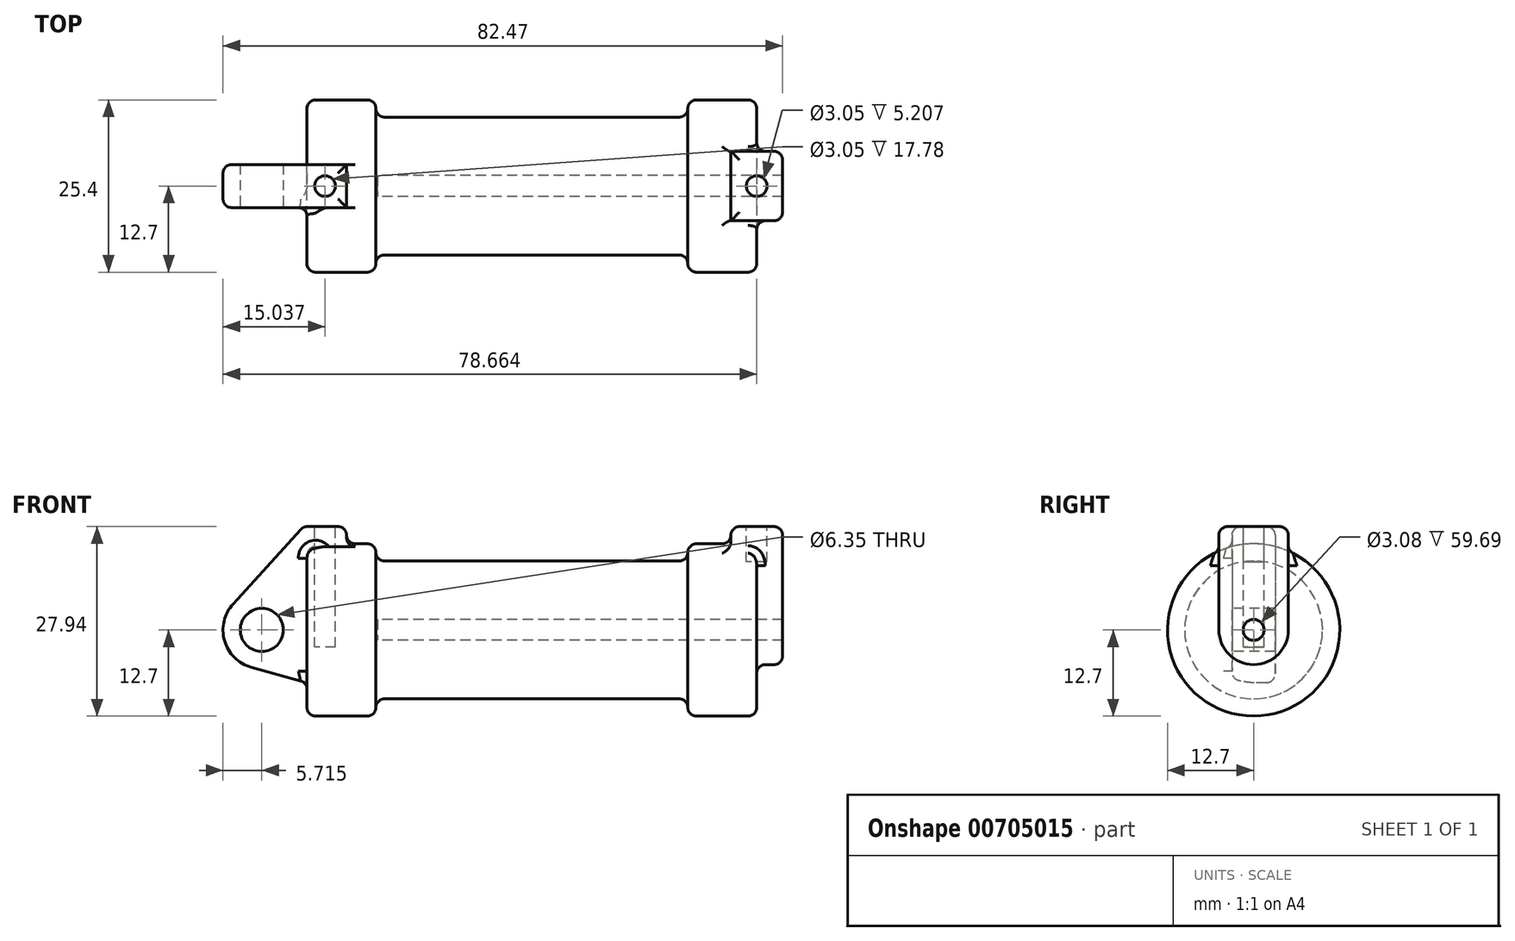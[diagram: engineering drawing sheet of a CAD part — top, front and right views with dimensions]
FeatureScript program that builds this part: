
annotation { "Feature Type Name" : "Feature", "Feature Type Description" : "" }
export const myFeature = defineFeature(function(context is Context, id is Id, definition is map)
    precondition{}
    {
        {
            var Q0;
            Q0=qCreatedBy(makeId("Front.planeOp"),FACE);
            var sketch = newSketch(context, id + "F0", { "sketchPlane" : qUnion([Q0])});
            skLineSegment(sketch, "E0", {"start": v(0, 0) * mm, "end": v(0, 12.7) * mm});
            skLineSegment(sketch, "E1", {"start": v(0, 12.7) * mm, "end": v(10.16, 12.7) * mm});
            skLineSegment(sketch, "E2", {"start": v(10.16, 12.7) * mm, "end": v(10.16, 10.16) * mm});
            skLineSegment(sketch, "E3", {"start": v(10.16, 10.16) * mm, "end": v(56.13, 10.16) * mm});
            skLineSegment(sketch, "E4", {"start": v(56.13, 10.16) * mm, "end": v(56.13, 12.7) * mm});
            skLineSegment(sketch, "E5", {"start": v(56.13, 12.7) * mm, "end": v(66.3, 12.7) * mm});
            skLineSegment(sketch, "E6", {"start": v(66.3, 12.7) * mm, "end": v(66.3, 0) * mm});
            skLineSegment(sketch, "E7", {"start": v(66.3, 0) * mm, "end": v(0, 0) * mm});
            skLineSegment(sketch, "E8", {"start": v(5.84, 15.24) * mm, "end": v(-0.5, 15.24) * mm});
            skLineSegment(sketch, "E9", {"start": v(-0.5, 15.24) * mm, "end": v(-10.88, 3.85) * mm});
            skLineSegment(sketch, "E10", {"start": v(0, 0) * mm, "end": v(-6.65, 0) * mm});
            skCircle(sketch, "E11", {"center": v(-6.65, 0) * mm, "radius": 5.72 * mm});
            skCircle(sketch, "E12", {"center": v(-6.65, 0) * mm, "radius": 3.18 * mm});
            skLineSegment(sketch, "E13", {"start": v(5.84, 15.24) * mm, "end": v(5.84, -9.4) * mm});
            skLineSegment(sketch, "E14", {"start": v(5.84, -9.4) * mm, "end": v(-8.18, -5.5) * mm});
            skSolve(sketch);
        }
        {
            var Q0;
            {var subQ0=sQuery(id+"F0.wireOp",EDGE,"E0");Q0=makeQuery(id+"F0.imprint","IMPRINT",FACE,{"disambiguationData":[TD([[makeQuery(id+"F0.imprint","IMPRINT",EDGE,{"derivedFrom":subQ0}),-1.0]])]});}
            var Q1;
            {var subQ0=sQuery(id+"F0.wireOp",EDGE,"E2");Q1=makeQuery(id+"F0.imprint","IMPRINT",FACE,{"disambiguationData":[TD([[makeQuery(id+"F0.imprint","IMPRINT",EDGE,{"derivedFrom":subQ0}),-1.0]])]});}
            var Q2;
            Q2=sQuery(id+"F0.wireOp",EDGE,"E7");
            revolve(context, id + "F1", {"entities" : qUnion([Q0, Q1]), "axis" : qUnion([Q2]), "revolveType" : RevolveType.FULL});
        }
        {
            var Q0;
            {var subQ1=sQuery(id+"F0.wireOp",EDGE,"E0");Q0=makeQuery(id+"F0.imprint","IMPRINT",FACE,{"disambiguationData":[TD([[makeQuery(id+"F0.imprint","IMPRINT",EDGE,{"derivedFrom":subQ1}),1.0]])]});}
            var Q1;
            {var subQ0=sQuery(id+"F0.wireOp",EDGE,"E14");Q1=makeQuery(id+"F0.imprint","IMPRINT",FACE,{"disambiguationData":[TD([[makeQuery(id+"F0.imprint","IMPRINT",EDGE,{"derivedFrom":subQ0}),-1.0]])]});}
            var Q2;
            {var subQ5=sQuery(id+"F0.wireOp",EDGE,"E12");Q2=makeQuery(id+"F0.imprint","IMPRINT",FACE,{"disambiguationData":[TD([[makeQuery(id+"F0.imprint","IMPRINT",EDGE,{"derivedFrom":subQ5}),-1.0]])]});}
            var Q3;
            {var subQ0=sQuery(id+"F0.wireOp",EDGE,"E0");Q3=makeQuery(id+"F0.imprint","IMPRINT",FACE,{"disambiguationData":[TD([[makeQuery(id+"F0.imprint","IMPRINT",EDGE,{"derivedFrom":subQ0}),-1.0]])]});}
            extrude(context, id + "F2", {"entities" : qUnion([Q0, Q1, Q2, Q3]), "operationType" : NewBodyOperationType.ADD, "oppositeDirection" : true, "depth" : 6.35 * mm, "offsetDistance" : 25.4 * mm, "symmetric" : true});
        }
        {
            var Q0;
            Q0=makeQuery(id+"F1.opRevolve","SWEPT_FACE",FACE,{"disambiguationData":[OSD([sQuery(id+"F0.wireOp",EDGE,"E6")])]});
            var sketch = newSketch(context, id + "F3", { "sketchPlane" : qUnion([Q0])});
            skCircle(sketch, "E15", {"center": v(0, 0) * mm, "radius": 1.54 * mm});
            skCircle(sketch, "E16", {"center": v(0, 0) * mm, "radius": 5.12 * mm});
            skLineSegment(sketch, "E17", {"start": v(-5.12, 0) * mm, "end": v(-5.12, 15.24) * mm});
            skLineSegment(sketch, "E18", {"start": v(5.12, 0) * mm, "end": v(5.12, 15.24) * mm});
            skLineSegment(sketch, "E19", {"start": v(5.12, 15.24) * mm, "end": v(-5.12, 15.24) * mm});
            skSolve(sketch);
        }
        {
            var Q0;
            Q0=makeQuery(id+"F3.imprint","IMPRINT",FACE,{"disambiguationData":[TD([[makeQuery(id+"F3.imprint","IMPRINT",EDGE,{"derivedFrom":sQuery(id+"F3.wireOp",EDGE,"E15")}),-1.0]])]});
            var Q1;
            {var subQ0=sQuery(id+"F3.wireOp",EDGE,"E17");var subQ1=sQuery(id+"F3.wireOp",EDGE,"E16");var subQ2=makeQuery(id+"F3.imprint","INTERSECT",VERTEX,{"derivedFrom":[subQ1,subQ0]});Q1=makeQuery(id+"F3.imprint","IMPRINT",FACE,{"disambiguationData":[TD([[makeQuery(id+"F3.imprint","IMPRINT",EDGE,{"disambiguationData":[TD([[subQ2,1.0]])],"derivedFrom":subQ1}),-1.0]])]});}
            var Q2;
            {var subQ0=sQuery(id+"F3.wireOp",EDGE,"E19");Q2=makeQuery(id+"F3.imprint","IMPRINT",FACE,{"disambiguationData":[TD([[makeQuery(id+"F3.imprint","IMPRINT",EDGE,{"derivedFrom":subQ0}),1.0]])]});}
            extrude(context, id + "F4", {"entities" : qUnion([Q0, Q1, Q2]), "operationType" : NewBodyOperationType.ADD, "depth" : 7.62 * mm, "offsetDistance" : 25.4 * mm, "symmetric" : true});
        }
        {
            var Q0;
            Q0=makeQuery(id+"F4.boolean.opBoolean","SPLIT",FACE,{"disambiguationData":[TD([makeQuery(id+"F4.opExtrude","SWEPT_FACE",FACE,{"disambiguationData":[OSD([sQuery(id+"F3.wireOp",EDGE,"E15")])]})])],"derivedFrom":makeQuery(id+"F1.opRevolve","SWEPT_FACE",FACE,{"disambiguationData":[OSD([sQuery(id+"F0.wireOp",EDGE,"E6")])]})});
            extrude(context, id + "F5", {"entities" : qUnion([Q0]), "operationType" : NewBodyOperationType.REMOVE, "oppositeDirection" : true, "depth" : 55.88 * mm, "offsetDistance" : 25.4 * mm});
        }
        {
            var Q0;
            Q0=makeQuery(id+"F2.opExtrude","SWEPT_FACE",FACE,{"disambiguationData":[OSD([sQuery(id+"F0.wireOp",EDGE,"E8")])]});
            var sketch = newSketch(context, id + "F6", { "sketchPlane" : qUnion([Q0])});
            skPoint(sketch, "E20.centerSnap0", {"position": v(2.67, 3.18) * mm});
            skCircle(sketch, "E21", {"center": v(2.67, 0) * mm, "radius": 1.52 * mm});
            skPoint(sketch, "E21.centerSnap0", {"position": v(-0.5, 0) * mm});
            skSolve(sketch);
        }
        {
            var Q0;
            Q0=makeQuery(id+"F4.opExtrude","SWEPT_FACE",FACE,{"disambiguationData":[OSD([sQuery(id+"F3.wireOp",EDGE,"E19")])]});
            var sketch = newSketch(context, id + "F7", { "sketchPlane" : qUnion([Q0])});
            skCircle(sketch, "E22", {"center": v(66.3, 0) * mm, "radius": 1.52 * mm});
            skPoint(sketch, "E22.centerSnap0", {"position": v(66.3, 5.12) * mm});
            skPoint(sketch, "E22.centerSnap1", {"position": v(62.48, 0) * mm});
            skSolve(sketch);
        }
        {
            var Q0;
            Q0=makeQuery(id+"F7.imprint","IMPRINT",FACE,{"disambiguationData":[TD([[makeQuery(id+"F7.imprint","IMPRINT",EDGE,{"derivedFrom":sQuery(id+"F7.wireOp",EDGE,"E22")}),1.0]])]});
            extrude(context, id + "F8", {"entities" : qUnion([Q0]), "operationType" : NewBodyOperationType.REMOVE, "oppositeDirection" : true, "depth" : 10.4 * mm, "offsetDistance" : 25.4 * mm, "symmetric" : true});
        }
        {
            var Q0;
            Q0=makeQuery(id+"F2.opExtrude","CAP_EDGE",EDGE,{"disambiguationData":[OSD([sQuery(id+"F0.wireOp",EDGE,"E9")])],"isStart":true});
            var Q1;
            Q1=makeQuery(id+"F2.opExtrude","CAP_EDGE",EDGE,{"disambiguationData":[OSD([sQuery(id+"F0.wireOp",EDGE,"E9")])],"isStart":false});
            var Q2;
            Q2=makeQuery(id+"F1.opRevolve","SWEPT_EDGE",EDGE,{"disambiguationData":[OSD([sQuery(id+"F0.wireOp",EDGE,"E0"),sQuery(id+"F0.wireOp",EDGE,"E1")])]});
            var Q3;
            Q3=makeQuery(id+"F2.opExtrude","CAP_EDGE",EDGE,{"disambiguationData":[OSD([sQuery(id+"F0.wireOp",EDGE,"E8")])],"isStart":true});
            var Q4;
            Q4=makeQuery(id+"F2.opExtrude","SWEPT_EDGE",EDGE,{"disambiguationData":[OSD([sQuery(id+"F0.wireOp",EDGE,"E8"),sQuery(id+"F0.wireOp",EDGE,"E13")])]});
            var Q5;
            Q5=makeQuery(id+"F2.opExtrude","CAP_EDGE",EDGE,{"disambiguationData":[OSD([sQuery(id+"F0.wireOp",EDGE,"E8")])],"isStart":false});
            var Q6;
            Q6=makeQuery(id+"F2.opExtrude","SWEPT_EDGE",EDGE,{"disambiguationData":[OSD([sQuery(id+"F0.wireOp",EDGE,"E8"),sQuery(id+"F0.wireOp",EDGE,"E9")])]});
            var Q7;
            Q7=makeQuery(id+"F1.opRevolve","SWEPT_EDGE",EDGE,{"disambiguationData":[OSD([sQuery(id+"F0.wireOp",EDGE,"E1"),sQuery(id+"F0.wireOp",EDGE,"E2")])]});
            var Q8;
            Q8=makeQuery(id+"F4.boolean.opBoolean","INTERSECT",EDGE,{"derivedFrom":[makeQuery(id+"F1.opRevolve","SWEPT_FACE",FACE,{"disambiguationData":[OSD([sQuery(id+"F0.wireOp",EDGE,"E6")])]}),makeQuery(id+"F4.opExtrude","SWEPT_FACE",FACE,{"disambiguationData":[OSD([sQuery(id+"F3.wireOp",EDGE,"E18")])]})]});
            var Q9;
            Q9=makeQuery(id+"F4.opExtrude","CAP_EDGE",EDGE,{"disambiguationData":[OSD([sQuery(id+"F3.wireOp",EDGE,"E18")])],"isStart":false});
            var Q10;
            Q10=makeQuery(id+"F4.opExtrude","CAP_EDGE",EDGE,{"disambiguationData":[OSD([sQuery(id+"F3.wireOp",EDGE,"E19")])],"isStart":false});
            var Q11;
            Q11=makeQuery(id+"F4.opExtrude","SWEPT_EDGE",EDGE,{"disambiguationData":[OSD([sQuery(id+"F3.wireOp",EDGE,"E18"),sQuery(id+"F3.wireOp",EDGE,"E19")])]});
            var Q12;
            Q12=makeQuery(id+"F4.opExtrude","CAP_EDGE",EDGE,{"disambiguationData":[OSD([sQuery(id+"F3.wireOp",EDGE,"E19")])],"isStart":true});
            var Q13;
            Q13=makeQuery(id+"F4.opExtrude","SWEPT_EDGE",EDGE,{"disambiguationData":[OSD([sQuery(id+"F3.wireOp",EDGE,"E17"),sQuery(id+"F3.wireOp",EDGE,"E19")])]});
            var Q14;
            Q14=makeQuery(id+"F4.boolean.opBoolean","INTERSECT",EDGE,{"derivedFrom":[makeQuery(id+"F1.opRevolve","SWEPT_FACE",FACE,{"disambiguationData":[OSD([sQuery(id+"F0.wireOp",EDGE,"E5")])]}),makeQuery(id+"F4.opExtrude","SWEPT_FACE",FACE,{"disambiguationData":[OSD([sQuery(id+"F3.wireOp",EDGE,"E17")])]})]});
            var Q15;
            Q15=makeQuery(id+"F4.boolean.opBoolean","INTERSECT",EDGE,{"derivedFrom":[makeQuery(id+"F1.opRevolve","SWEPT_FACE",FACE,{"disambiguationData":[OSD([sQuery(id+"F0.wireOp",EDGE,"E5")])]}),makeQuery(id+"F4.opExtrude","CAP_FACE",FACE,{"disambiguationData":[OSD([sQuery(id+"F3.wireOp",EDGE,"E15"),sQuery(id+"F3.wireOp",EDGE,"E16"),sQuery(id+"F3.wireOp",EDGE,"E17"),sQuery(id+"F3.wireOp",EDGE,"E18"),sQuery(id+"F3.wireOp",EDGE,"E19")])],"isStart":true})]});
            var Q16;
            Q16=makeQuery(id+"F4.boolean.opBoolean","INTERSECT",EDGE,{"derivedFrom":[makeQuery(id+"F1.opRevolve","SWEPT_FACE",FACE,{"disambiguationData":[OSD([sQuery(id+"F0.wireOp",EDGE,"E5")])]}),makeQuery(id+"F4.opExtrude","SWEPT_FACE",FACE,{"disambiguationData":[OSD([sQuery(id+"F3.wireOp",EDGE,"E18")])]})]});
            var Q17;
            Q17=makeQuery(id+"F2.boolean.opBoolean","INTERSECT",EDGE,{"derivedFrom":[makeQuery(id+"F1.opRevolve","SWEPT_FACE",FACE,{"disambiguationData":[OSD([sQuery(id+"F0.wireOp",EDGE,"E0")])]}),makeQuery(id+"F2.opExtrude","CAP_FACE",FACE,{"disambiguationData":[OSD([sQuery(id+"F0.wireOp",EDGE,"E8"),sQuery(id+"F0.wireOp",EDGE,"E9"),sQuery(id+"F0.wireOp",EDGE,"E11"),sQuery(id+"F0.wireOp",EDGE,"E12"),sQuery(id+"F0.wireOp",EDGE,"E13"),sQuery(id+"F0.wireOp",EDGE,"E14")])],"isStart":true})]});
            var Q18;
            Q18=makeQuery(id+"F1.opRevolve","SWEPT_EDGE",EDGE,{"disambiguationData":[OSD([sQuery(id+"F0.wireOp",EDGE,"E3"),sQuery(id+"F0.wireOp",EDGE,"E4")])]});
            var Q19;
            Q19=makeQuery(id+"F1.opRevolve","SWEPT_EDGE",EDGE,{"disambiguationData":[OSD([sQuery(id+"F0.wireOp",EDGE,"E4"),sQuery(id+"F0.wireOp",EDGE,"E5")])]});
            var Q20;
            Q20=makeQuery(id+"F1.opRevolve","SWEPT_EDGE",EDGE,{"disambiguationData":[OSD([sQuery(id+"F0.wireOp",EDGE,"E2"),sQuery(id+"F0.wireOp",EDGE,"E3")])]});
            var Q21;
            Q21=makeQuery(id+"F2.boolean.opBoolean","INTERSECT",EDGE,{"derivedFrom":[makeQuery(id+"F1.opRevolve","SWEPT_FACE",FACE,{"disambiguationData":[OSD([sQuery(id+"F0.wireOp",EDGE,"E1")])]}),makeQuery(id+"F2.opExtrude","SWEPT_FACE",FACE,{"disambiguationData":[OSD([sQuery(id+"F0.wireOp",EDGE,"E13")])]})]});
            var Q22;
            Q22=makeQuery(id+"F1.opRevolve","SWEPT_EDGE",EDGE,{"disambiguationData":[OSD([sQuery(id+"F0.wireOp",EDGE,"E5"),sQuery(id+"F0.wireOp",EDGE,"E6")])]});
            fillet(context, id + "F9", {"entities" : qUnion([Q0, Q1, Q2, Q3, Q4, Q5, Q6, Q7, Q8, Q9, Q10, Q11, Q12, Q13, Q14, Q15, Q16, Q17, Q18, Q19, Q20, Q21, Q22]), "radius" : 1.27 * mm, "tangentPropagation" : true, "allowEdgeOverflow" : false});
        }
        {
            var Q0;
            Q0=makeQuery(id+"F6.imprint","IMPRINT",FACE,{"disambiguationData":[TD([[makeQuery(id+"F6.imprint","IMPRINT",EDGE,{"derivedFrom":sQuery(id+"F6.wireOp",EDGE,"E21")}),1.0]])]});
            extrude(context, id + "F10", {"entities" : qUnion([Q0]), "operationType" : NewBodyOperationType.REMOVE, "oppositeDirection" : true, "depth" : 17.78 * mm, "offsetDistance" : 25.4 * mm});
        }
    });
